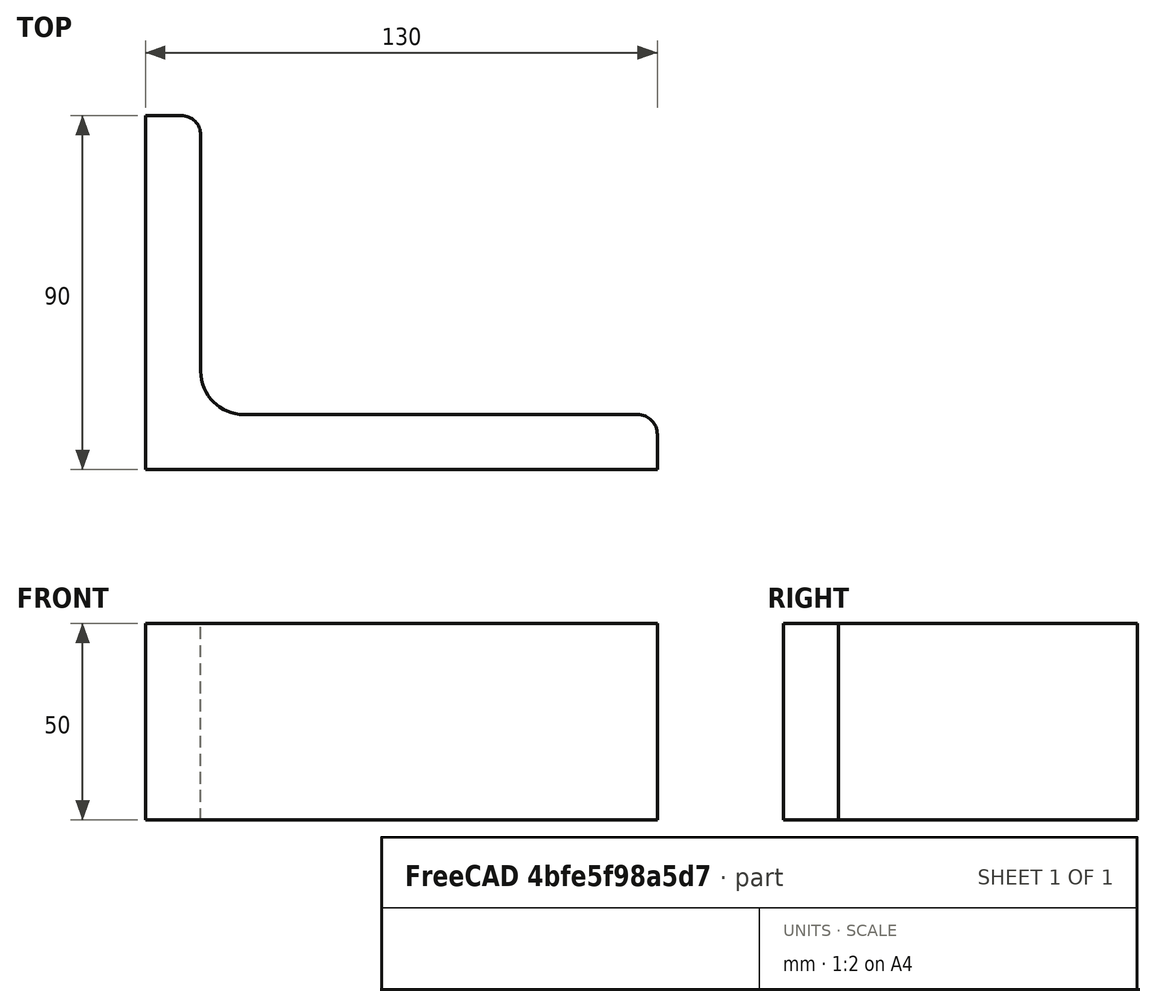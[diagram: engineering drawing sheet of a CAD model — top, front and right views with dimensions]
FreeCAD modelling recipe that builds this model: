
FCSTD DOCUMENT  (FreeCAD 0.15R4671 (Git))
Label: Angle Bar 130x90x14 EN10056 S235JR
License: All rights reserved
LicenseURL: http://en.wikipedia.org/wiki/All_rights_reserved
objects: Sketcher::SketchObject×1, Part::Extrusion×1
note: 2 computed .brp shape members not serialized (recipe doc carries the construction recipe); baked Part::Feature solids carry a one-line shape summary decoded from their .brp

FEATURE [Sketcher::SketchObject] Sketch
  sketch-geometry (9):
    g0: LineSegment StartX=0 StartY=0 StartZ=0 EndX=130 EndY=0 EndZ=0
    g1: LineSegment StartX=130 StartY=0 StartZ=0 EndX=130 EndY=9 EndZ=0
    g2: LineSegment StartX=125 StartY=14 StartZ=0 EndX=25 EndY=14 EndZ=0
    g3: LineSegment StartX=0 StartY=0 StartZ=0 EndX=0 EndY=90 EndZ=0
    g4: LineSegment StartX=0 StartY=90 StartZ=0 EndX=9 EndY=90 EndZ=0
    g5: LineSegment StartX=14 StartY=85 StartZ=0 EndX=14 EndY=25 EndZ=0
    g6: ArcOfCircle CenterX=25 CenterY=25 CenterZ=0 NormalX=0 NormalY=0 NormalZ=1 Radius=11 StartAngle=3.14159 EndAngle=4.71239
    g7: ArcOfCircle CenterX=9 CenterY=85 CenterZ=0 NormalX=0 NormalY=0 NormalZ=1 Radius=5 StartAngle=0 EndAngle=1.5708
    g8: ArcOfCircle CenterX=125 CenterY=9 CenterZ=0 NormalX=0 NormalY=0 NormalZ=1 Radius=5 StartAngle=0 EndAngle=1.5708
  constraints (23):
    c: Coincident(g0,g-1)
    c: Horizontal(g0)
    c: Coincident(g1,g0)
    c: Vertical(g1)
    c: Horizontal(g2)
    c: Coincident(g3,g-1)
    c: Vertical(g3)
    c: Coincident(g4,g3)
    c: Horizontal(g4)
    c: Vertical(g5)
    c: Tangent(g5,g6) = -1.5708
    c: Tangent(g2,g6) = 1.5708
    c: Tangent(g4,g7) = 1.5708
    c: Tangent(g5,g7) = 1.5708
    c: Tangent(g2,g8) = -1.5708
    c: Tangent(g1,g8) = -1.5708
    c: DistanceX(g0) = 130
    c: DistanceY(g3) = 90
    c: DistanceY(g0,g2) = 14
    c: DistanceX(g3,g5) = 14
    c: Radius(g6) = 11
    c: Radius(g8) = 5
    c: Radius(g7) = 5
FEATURE [Part::Extrusion] Extrude  label="Angle Bar 130x90x14 EN10056 S235JR"
  Base = -> Sketch
  Dir = (0,0,50)
  Solid = true
